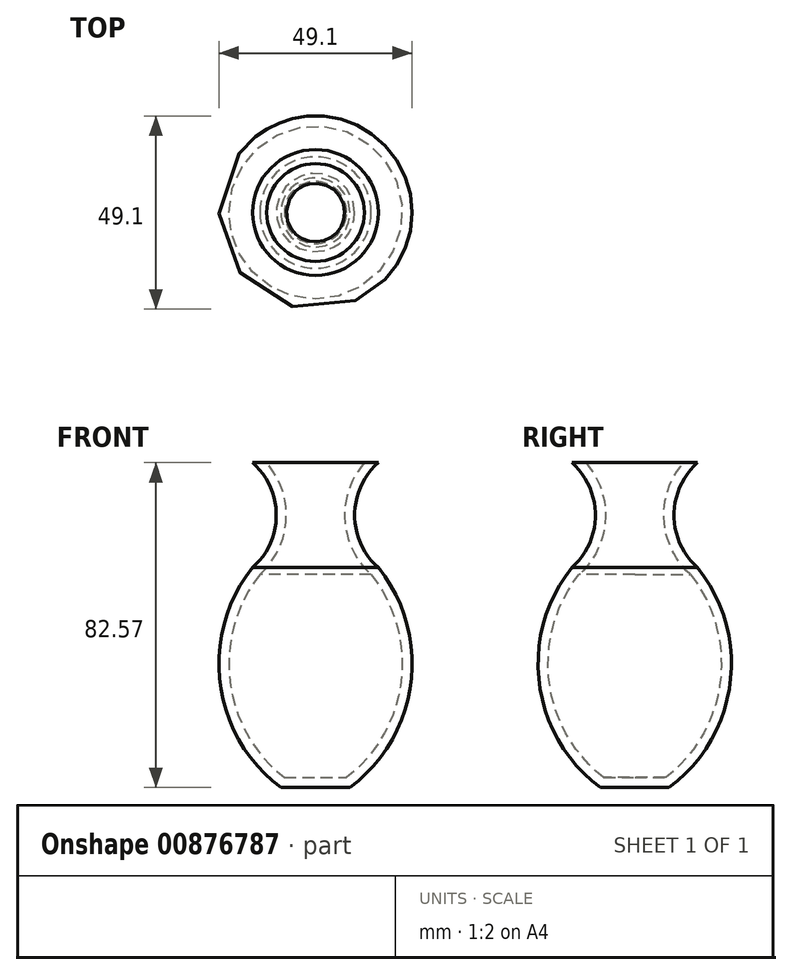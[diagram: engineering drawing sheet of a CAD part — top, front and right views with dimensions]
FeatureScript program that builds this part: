
annotation { "Feature Type Name" : "Feature", "Feature Type Description" : "" }
export const myFeature = defineFeature(function(context is Context, id is Id, definition is map)
    precondition{}
    {
        {
            var Q0;
            Q0=qCreatedBy(makeId("Front.planeOp"),FACE);
            var sketch = newSketch(context, id + "F0", { "sketchPlane" : qUnion([Q0])});
            skArc(sketch, "E0", {"start": v(8.75, -38.98) * mm, "mid": v(24.22, -12.58) * mm, "end": v(16, 16.9) * mm});
            skArc(sketch, "E1.MirrorCS", {"start": v(-8.75, -38.98) * mm, "mid": v(-24.22, -12.58) * mm, "end": v(-16, 16.9) * mm});
            skArc(sketch, "E2", {"start": v(16, 43.59) * mm, "mid": v(9.96, 30.24) * mm, "end": v(16, 16.9) * mm});
            skArc(sketch, "E3.MirrorCS", {"start": v(-16, 43.59) * mm, "mid": v(-9.96, 30.24) * mm, "end": v(-16, 16.9) * mm});
            skLineSegment(sketch, "E4", {"start": v(8.75, -38.98) * mm, "end": v(-8.75, -38.98) * mm});
            skLineSegment(sketch, "E5", {"start": v(16, 43.59) * mm, "end": v(-16, 43.59) * mm});
            skLineSegment(sketch, "E6", {"start": v(0, 43.59) * mm, "end": v(0, -38.98) * mm});
            skSolve(sketch);
        }
        {
            var Q0;
            Q0=makeQuery(id+"F0.imprint","IMPRINT",FACE,{"disambiguationData":[TD([[makeQuery(id+"F0.imprint","IMPRINT",EDGE,{"derivedFrom":sQuery(id+"F0.wireOp",EDGE,"E0")}),1.0]])]});
            var Q1;
            Q1=sQuery(id+"F0.wireOp",EDGE,"E6");
            revolve(context, id + "F1", {"surfaceOperationType" : NewSurfaceOperationType.NEW, "entities" : qUnion([Q0]), "axis" : qUnion([Q1]), "revolveType" : RevolveType.SYMMETRIC, "angle" : 360 * degree});
        }
        {
            var Q0;
            Q0=makeQuery(id+"F1.opRevolve","SWEPT_FACE",FACE,{"disambiguationData":[OSD([sQuery(id+"F0.wireOp",EDGE,"E5")])]});
            shell(context, id + "F2", {"entities" : qUnion([Q0]), "thickness" : 2.54 * mm});
        }
    });
